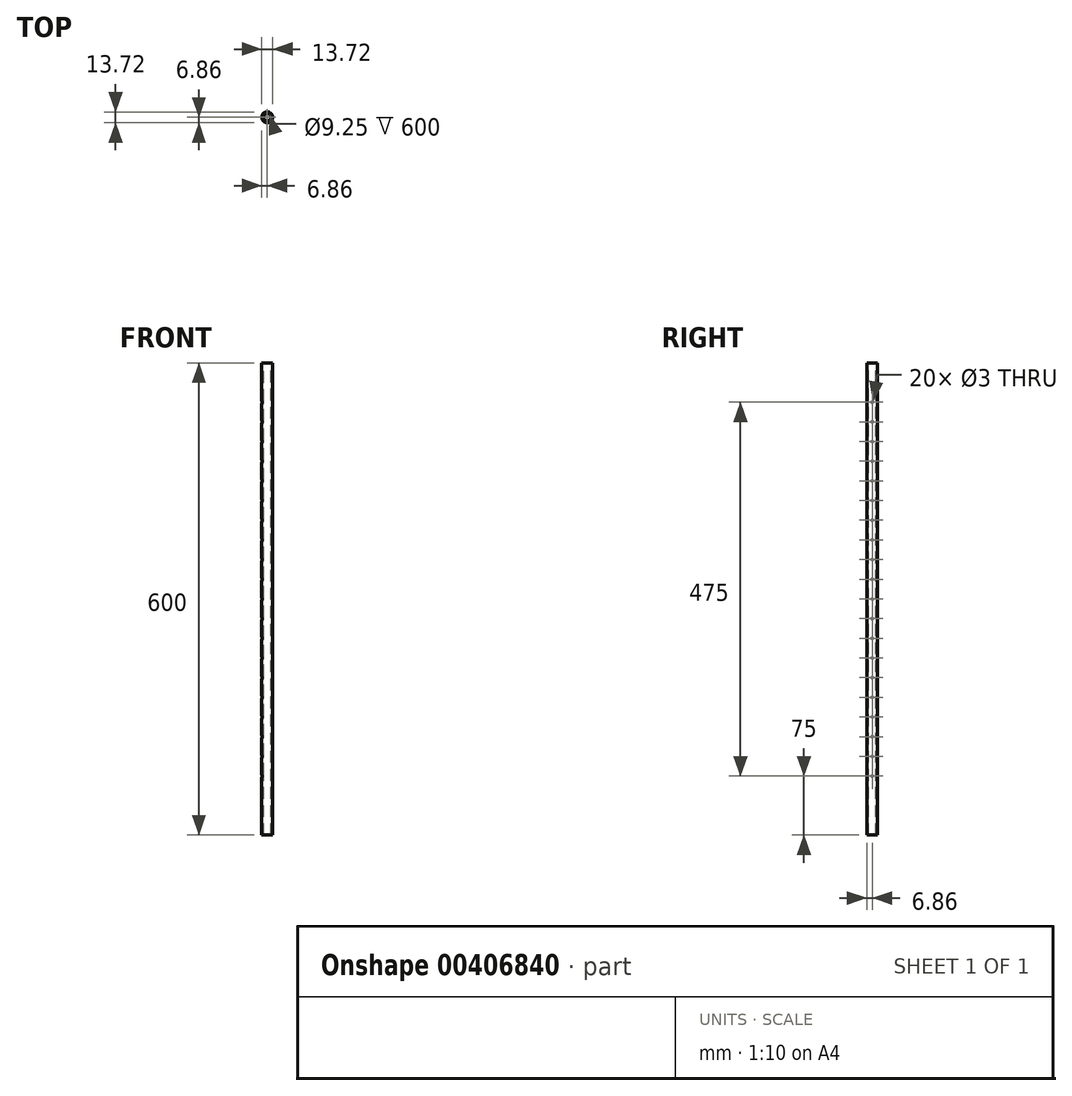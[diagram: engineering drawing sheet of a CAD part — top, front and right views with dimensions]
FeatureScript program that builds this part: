
annotation { "Feature Type Name" : "Feature", "Feature Type Description" : "" }
export const myFeature = defineFeature(function(context is Context, id is Id, definition is map)
    precondition{}
    {
        {
            var Q0;
            Q0=qCreatedBy(makeId("Top.planeOp"),FACE);
            var sketch = newSketch(context, id + "F0", { "sketchPlane" : qUnion([Q0])});
            skCircle(sketch, "E0", {"center": v(0, 0) * mm, "radius": 6.86 * mm});
            skCircle(sketch, "E1", {"center": v(0, 0) * mm, "radius": 4.62 * mm});
            skSolve(sketch);
        }
        {
            var Q0;
            Q0 = qSketchRegion(id + "F0", true);
            extrude(context, id + "F1", {"entities" : qUnion([Q0]), "oppositeDirection" : true, "depth" : 600 * mm});
        }
        {
            var Q0;
            Q0=qCreatedBy(makeId("Right.planeOp"),FACE);
            var sketch = newSketch(context, id + "F2", { "sketchPlane" : qUnion([Q0])});
            skCircle(sketch, "E2", {"center": v(0, -50) * mm, "radius": 1.5 * mm});
            skCircle(sketch, "E3.1.0.0", {"center": v(0, -75) * mm, "radius": 1.5 * mm});
            skCircle(sketch, "E3.2.0.0", {"center": v(0, -100) * mm, "radius": 1.5 * mm});
            skCircle(sketch, "E3.3.0.0", {"center": v(0, -125) * mm, "radius": 1.5 * mm});
            skCircle(sketch, "E3.4.0.0", {"center": v(0, -150) * mm, "radius": 1.5 * mm});
            skCircle(sketch, "E3.5.0.0", {"center": v(0, -175) * mm, "radius": 1.5 * mm});
            skCircle(sketch, "E3.6.0.0", {"center": v(0, -200) * mm, "radius": 1.5 * mm});
            skCircle(sketch, "E3.7.0.0", {"center": v(0, -225) * mm, "radius": 1.5 * mm});
            skCircle(sketch, "E3.8.0.0", {"center": v(0, -250) * mm, "radius": 1.5 * mm});
            skCircle(sketch, "E3.9.0.0", {"center": v(0, -275) * mm, "radius": 1.5 * mm});
            skCircle(sketch, "E3.10.0.0", {"center": v(0, -300) * mm, "radius": 1.5 * mm});
            skCircle(sketch, "E3.11.0.0", {"center": v(0, -325) * mm, "radius": 1.5 * mm});
            skCircle(sketch, "E3.12.0.0", {"center": v(0, -350) * mm, "radius": 1.5 * mm});
            skCircle(sketch, "E3.13.0.0", {"center": v(0, -375) * mm, "radius": 1.5 * mm});
            skCircle(sketch, "E3.14.0.0", {"center": v(0, -400) * mm, "radius": 1.5 * mm});
            skCircle(sketch, "E3.15.0.0", {"center": v(0, -425) * mm, "radius": 1.5 * mm});
            skCircle(sketch, "E3.16.0.0", {"center": v(0, -450) * mm, "radius": 1.5 * mm});
            skCircle(sketch, "E3.17.0.0", {"center": v(0, -475) * mm, "radius": 1.5 * mm});
            skCircle(sketch, "E3.18.0.0", {"center": v(0, -500) * mm, "radius": 1.5 * mm});
            skCircle(sketch, "E3.19.0.0", {"center": v(0, -525) * mm, "radius": 1.5 * mm});
            skLineSegment(sketch, "E3.direction1", {"start": v(0, -50) * mm, "end": v(0, -75) * mm, "construction": true});
            skSolve(sketch);
        }
        {
            var Q0;
            Q0 = qSketchRegion(id + "F2", true);
            extrude(context, id + "F3", {"entities" : qUnion([Q0]), "operationType" : NewBodyOperationType.REMOVE, "endBound" : BoundingType.THROUGH_ALL, "oppositeDirection" : true, "depth" : 25 * mm});
        }
    });
